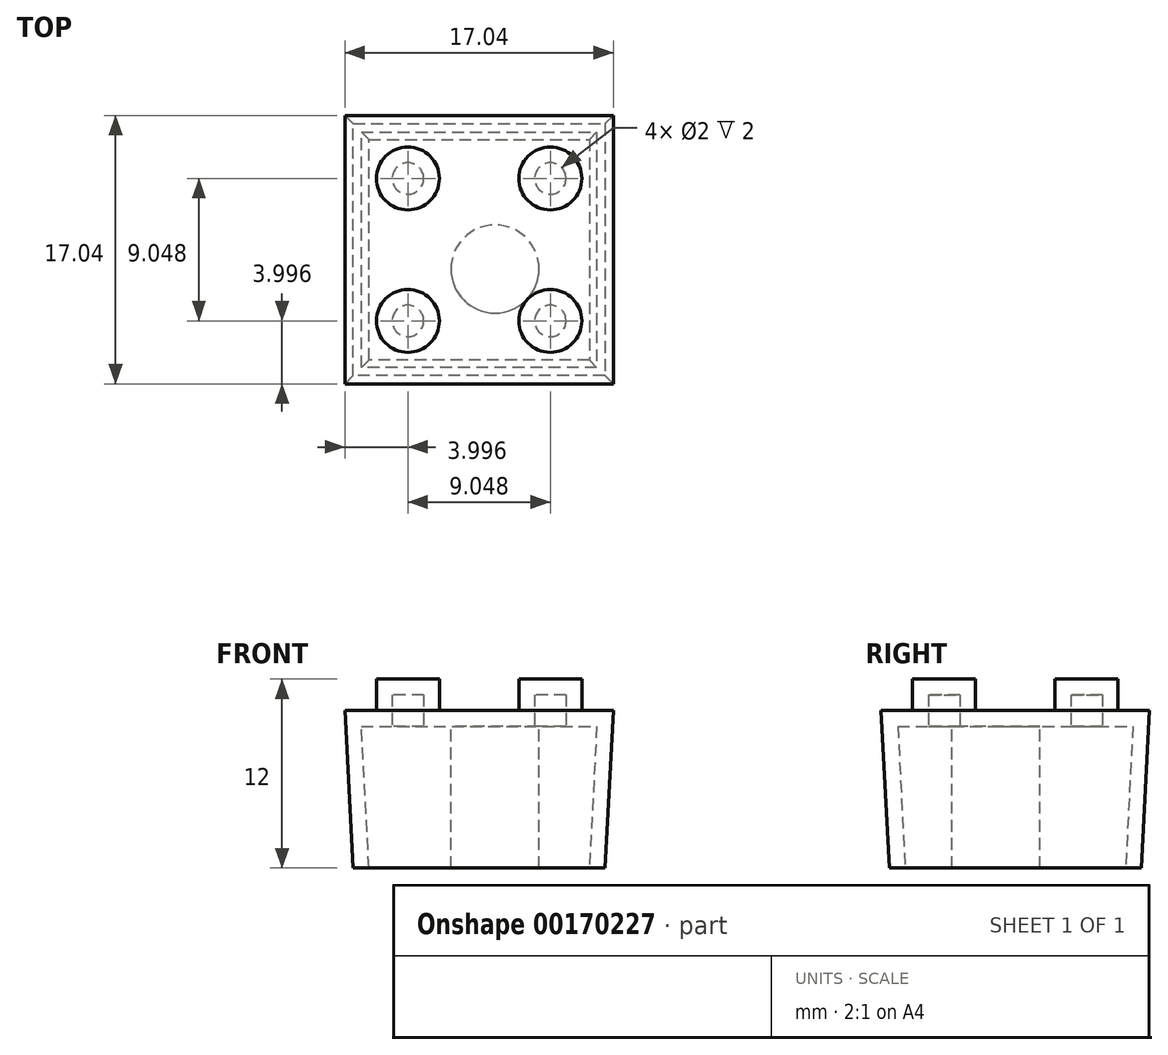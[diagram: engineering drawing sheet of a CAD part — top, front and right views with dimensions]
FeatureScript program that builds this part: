
annotation { "Feature Type Name" : "Feature", "Feature Type Description" : "" }
export const myFeature = defineFeature(function(context is Context, id is Id, definition is map)
    precondition{}
    {
        {
            var Q0;
            Q0=qCreatedBy(makeId("Top.planeOp"),FACE);
            var sketch = newSketch(context, id + "F0", { "sketchPlane" : qUnion([Q0])});
            skLineSegment(sketch, "E0.bottom", {"start": v(-8, 8) * mm, "end": v(8, 8) * mm});
            skLineSegment(sketch, "E0.top", {"start": v(-8, -8) * mm, "end": v(8, -8) * mm});
            skLineSegment(sketch, "E0.left", {"start": v(-8, 8) * mm, "end": v(-8, -8) * mm});
            skLineSegment(sketch, "E0.right", {"start": v(8, 8) * mm, "end": v(8, -8) * mm});
            skPoint(sketch, "E0.middle", {"position": v(0, 0) * mm});
            skSolve(sketch);
        }
        {
            var Q0;
            Q0=makeQuery(id+"F0.imprint","IMPRINT",FACE,{"disambiguationData":[TD([[makeQuery(id+"F0.imprint","IMPRINT",EDGE,{"derivedFrom":sQuery(id+"F0.wireOp",EDGE,"E0.bottom")}),-1.0]])]});
            extrude(context, id + "F1", {"entities" : qUnion([Q0]), "depth" : 10 * mm, "hasDraft" : true, "draftAngle" : 3 * degree});
        }
        {
            var Q0;
            Q0=makeQuery(id+"F1.opExtrude","CAP_FACE",FACE,{"disambiguationData":[OSD([sQuery(id+"F0.wireOp",EDGE,"E0.bottom"),sQuery(id+"F0.wireOp",EDGE,"E0.top"),sQuery(id+"F0.wireOp",EDGE,"E0.left"),sQuery(id+"F0.wireOp",EDGE,"E0.right")])],"isStart":false});
            var sketch = newSketch(context, id + "F2", { "sketchPlane" : qUnion([Q0])});
            skCircle(sketch, "E1", {"center": v(-4.52, 4.52) * mm, "radius": 2 * mm});
            skCircle(sketch, "E2.MirrorC", {"center": v(4.52, 4.52) * mm, "radius": 2 * mm});
            skCircle(sketch, "E3.MirrorC", {"center": v(4.52, -4.52) * mm, "radius": 2 * mm});
            skCircle(sketch, "E4.MirrorC", {"center": v(-4.52, -4.52) * mm, "radius": 2 * mm});
            skSolve(sketch);
        }
        {
            var Q0;
            Q0 = qSketchRegion(id + "F2", true);
            extrude(context, id + "F3", {"entities" : qUnion([Q0]), "operationType" : NewBodyOperationType.ADD, "depth" : 2 * mm});
        }
        {
            var Q0;
            Q0=makeQuery(id+"F1.opExtrude","CAP_FACE",FACE,{"disambiguationData":[OSD([sQuery(id+"F0.wireOp",EDGE,"E0.bottom"),sQuery(id+"F0.wireOp",EDGE,"E0.top"),sQuery(id+"F0.wireOp",EDGE,"E0.left"),sQuery(id+"F0.wireOp",EDGE,"E0.right")])],"isStart":true});
            shell(context, id + "F4", {"entities" : qUnion([Q0]), "thickness" : 1 * mm});
        }
        {
            var Q0;
            Q0=makeQuery(id+"F4.opShell","OFFSET_FACE",FACE,{"disambiguationData":[OSD([sQuery(id+"F0.wireOp",EDGE,"E0.bottom"),sQuery(id+"F0.wireOp",EDGE,"E0.top"),sQuery(id+"F0.wireOp",EDGE,"E0.left"),sQuery(id+"F0.wireOp",EDGE,"E0.right")])]});
            var sketch = newSketch(context, id + "F5", { "sketchPlane" : qUnion([Q0])});
            skCircle(sketch, "E5", {"center": v(1, 1.23) * mm, "radius": 2.8 * mm});
            skSolve(sketch);
        }
        {
            var Q0;
            Q0 = qSketchRegion(id + "F5", true);
            extrude(context, id + "F6", {"entities" : qUnion([Q0]), "operationType" : NewBodyOperationType.ADD, "depth" : 9 * mm});
        }
    });
